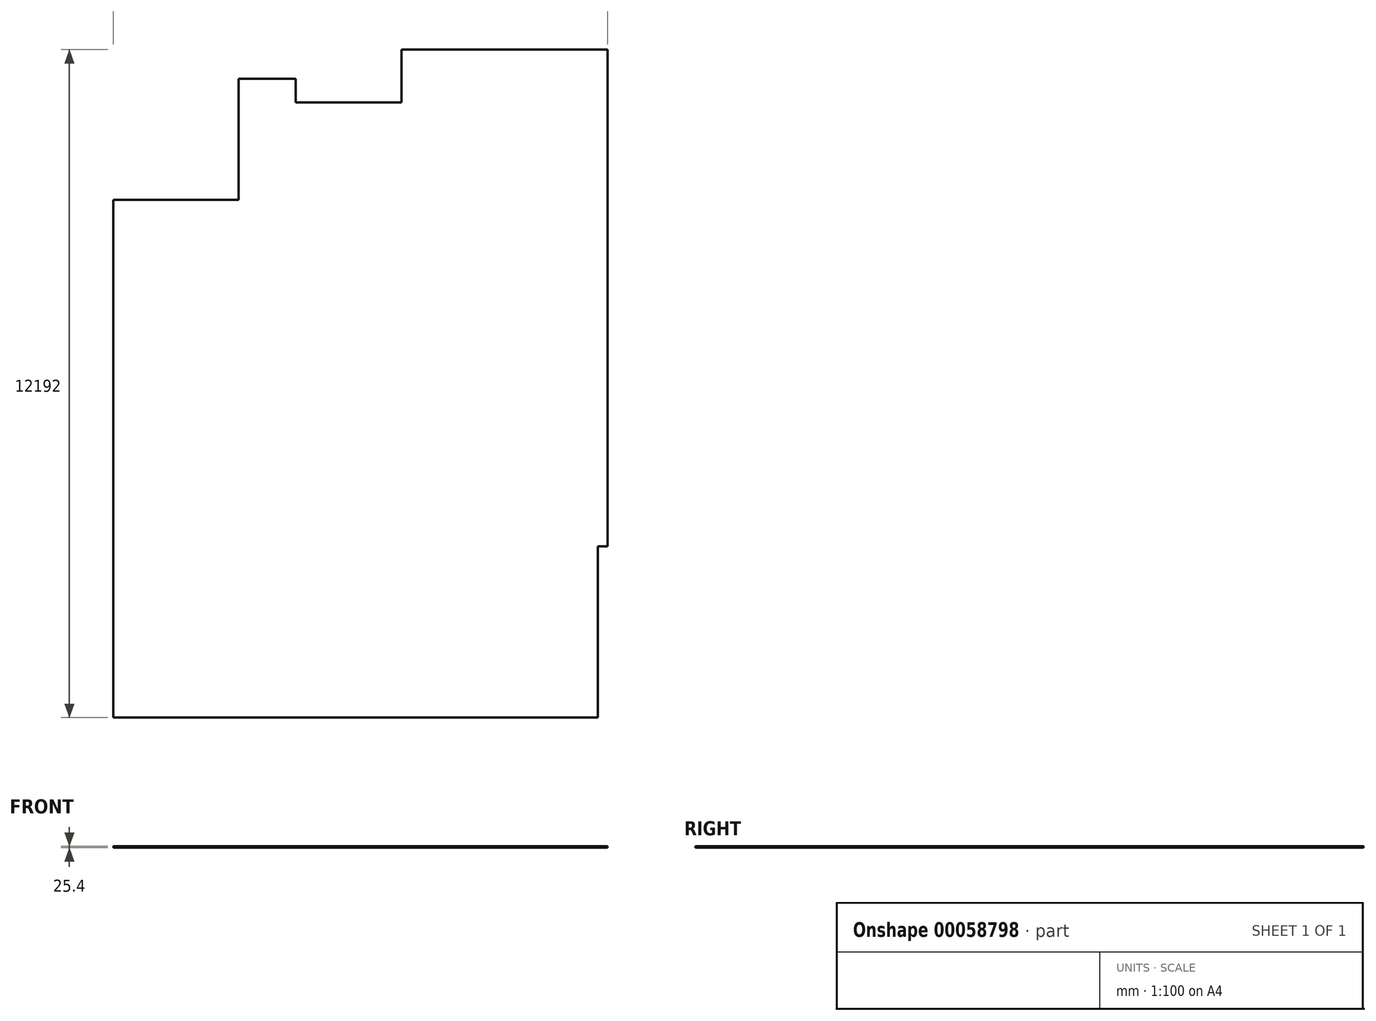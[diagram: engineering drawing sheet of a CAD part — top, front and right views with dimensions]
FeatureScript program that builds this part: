
annotation { "Feature Type Name" : "Feature", "Feature Type Description" : "" }
export const myFeature = defineFeature(function(context is Context, id is Id, definition is map)
    precondition{}
    {
        {
            var Q0;
            Q0=qCreatedBy(makeId("Top.planeOp"),FACE);
            var sketch = newSketch(context, id + "F0", { "sketchPlane" : qUnion([Q0])});
            skLineSegment(sketch, "E0.bottom", {"start": v(0, 0) * mm, "end": v(4749.8, 0) * mm});
            skLineSegment(sketch, "E0.left", {"start": v(0, 0) * mm, "end": v(0, 6604) * mm});
            skLineSegment(sketch, "E1", {"start": v(4749.8, 0) * mm, "end": v(4749.8, 4013.2) * mm});
            skLineSegment(sketch, "E2", {"start": v(0, 6604) * mm, "end": v(4038.6, 6604) * mm});
            skLineSegment(sketch, "E3", {"start": v(4038.6, 8432.8) * mm, "end": v(5257.8, 8432.8) * mm});
            skLineSegment(sketch, "E4", {"start": v(9017, 12192) * mm, "end": v(9017, 10972.8) * mm});
            skLineSegment(sketch, "E5", {"start": v(6451.6, 10972.8) * mm, "end": v(6451.6, 8407.4) * mm});
            skLineSegment(sketch, "E6", {"start": v(6451.6, 8407.4) * mm, "end": v(9017, 8407.4) * mm});
            skLineSegment(sketch, "E7", {"start": v(9017, 8407.4) * mm, "end": v(9017, 5638.8) * mm});
            skLineSegment(sketch, "E8", {"start": v(9017, 5638.8) * mm, "end": v(6451.6, 5638.8) * mm});
            skLineSegment(sketch, "E9", {"start": v(6451.6, 5638.8) * mm, "end": v(6451.6, 4013.2) * mm});
            skLineSegment(sketch, "E10", {"start": v(4749.8, 0) * mm, "end": v(8839.2, 0) * mm});
            skLineSegment(sketch, "E11", {"start": v(8839.2, 0) * mm, "end": v(8839.2, 3124.2) * mm});
            skLineSegment(sketch, "E12", {"start": v(8839.2, 3124.2) * mm, "end": v(7289.8, 3124.2) * mm});
            skLineSegment(sketch, "E13", {"start": v(7289.8, 3124.2) * mm, "end": v(7289.8, 4013.2) * mm});
            skLineSegment(sketch, "E14", {"start": v(9017, 5638.8) * mm, "end": v(9017, 3124.2) * mm});
            skLineSegment(sketch, "E15", {"start": v(8839.2, 3124.2) * mm, "end": v(9017, 3124.2) * mm});
            skLineSegment(sketch, "E16", {"start": v(7289.8, 4013.2) * mm, "end": v(9017, 4013.2) * mm});
            skLineSegment(sketch, "E17", {"start": v(0, 6604) * mm, "end": v(0, 9448.8) * mm});
            skLineSegment(sketch, "E18", {"start": v(3784.6, 9448.8) * mm, "end": v(3784.6, 8305.8) * mm});
            skLineSegment(sketch, "E19", {"start": v(3784.6, 8305.8) * mm, "end": v(4038.6, 8305.8) * mm});
            skLineSegment(sketch, "E20", {"start": v(5257.8, 11226.8) * mm, "end": v(3327.4, 11226.8) * mm});
            skLineSegment(sketch, "E21", {"start": v(3327.4, 11226.8) * mm, "end": v(3327.4, 11658.6) * mm});
            skLineSegment(sketch, "E22", {"start": v(3327.4, 11658.6) * mm, "end": v(2286, 11658.6) * mm});
            skLineSegment(sketch, "E23", {"start": v(2286, 11658.6) * mm, "end": v(2286, 9448.8) * mm});
            skLineSegment(sketch, "E24", {"start": v(3784.6, 9448.8) * mm, "end": v(5257.8, 9448.8) * mm});
            skLineSegment(sketch, "E25", {"start": v(7340.6, 8407.4) * mm, "end": v(7340.6, 9321.8) * mm});
            skLineSegment(sketch, "E26", {"start": v(7340.6, 9321.8) * mm, "end": v(6451.6, 9321.8) * mm});
            skLineSegment(sketch, "E27", {"start": v(7340.6, 9321.8) * mm, "end": v(7340.6, 10972.8) * mm});
            skLineSegment(sketch, "E28", {"start": v(9017, 10972.8) * mm, "end": v(9017, 8407.4) * mm});
            skLineSegment(sketch, "E29", {"start": v(4038.6, 8305.8) * mm, "end": v(4038.6, 7569.2) * mm});
            skLineSegment(sketch, "E30", {"start": v(4038.6, 6604) * mm, "end": v(4038.6, 6934.2) * mm});
            skLineSegment(sketch, "E31", {"start": v(4038.6, 8432.8) * mm, "end": v(4038.6, 8305.8) * mm});
            skLineSegment(sketch, "E32", {"start": v(4749.8, 4013.2) * mm, "end": v(5003.8, 4013.2) * mm});
            skLineSegment(sketch, "E33", {"start": v(6451.6, 4013.2) * mm, "end": v(5791.2, 4013.2) * mm});
            skLineSegment(sketch, "E34", {"start": v(6451.6, 4013.2) * mm, "end": v(6629.4, 4013.2) * mm});
            skLineSegment(sketch, "E35", {"start": v(0, 9448.8) * mm, "end": v(3073.4, 9448.8) * mm});
            skLineSegment(sketch, "E36", {"start": v(5257.8, 8432.8) * mm, "end": v(5257.8, 10337.8) * mm});
            skLineSegment(sketch, "E37", {"start": v(5257.8, 12192) * mm, "end": v(5257.8, 11023.6) * mm});
            skLineSegment(sketch, "E38", {"start": v(8077.2, 10972.8) * mm, "end": v(6451.6, 10972.8) * mm});
            skLineSegment(sketch, "E39", {"start": v(5257.8, 12192) * mm, "end": v(8077.2, 12192) * mm});
            skLineSegment(sketch, "E40", {"start": v(8077.2, 12192) * mm, "end": v(9017, 12192) * mm});
            skLineSegment(sketch, "E41", {"start": v(6451.6, 8407.4) * mm, "end": v(6451.6, 7747) * mm});
            skLineSegment(sketch, "E42", {"start": v(6451.6, 7747) * mm, "end": v(8356.6, 7747) * mm});
            skLineSegment(sketch, "E43", {"start": v(8356.6, 7747) * mm, "end": v(8356.6, 5638.8) * mm});
            skSolve(sketch);
        }
        {
            var Q0;
            Q0=makeQuery(id+"F0.imprint","IMPRINT",FACE,{"disambiguationData":[TD([[makeQuery(id+"F0.imprint","IMPRINT",EDGE,{"derivedFrom":sQuery(id+"F0.wireOp",EDGE,"E0.bottom")}),1.0]])]});
            var Q1;
            {var subQ1=sQuery(id+"F0.wireOp",EDGE,"E3");Q1=makeQuery(id+"F0.imprint","IMPRINT",FACE,{"disambiguationData":[TD([[makeQuery(id+"F0.imprint","IMPRINT",EDGE,{"derivedFrom":subQ1}),1.0]])]});}
            var Q2;
            {var subQ3=sQuery(id+"F0.wireOp",EDGE,"E26");Q2=makeQuery(id+"F0.imprint","IMPRINT",FACE,{"disambiguationData":[TD([[makeQuery(id+"F0.imprint","IMPRINT",EDGE,{"derivedFrom":subQ3}),-1.0]])]});}
            var Q3;
            {var subQ4=sQuery(id+"F0.wireOp",EDGE,"E25");Q3=makeQuery(id+"F0.imprint","IMPRINT",FACE,{"disambiguationData":[TD([[makeQuery(id+"F0.imprint","IMPRINT",EDGE,{"derivedFrom":subQ4}),1.0]])]});}
            var Q4;
            {var subQ1=sQuery(id+"F0.wireOp",EDGE,"E7");Q4=makeQuery(id+"F0.imprint","IMPRINT",FACE,{"disambiguationData":[TD([[makeQuery(id+"F0.imprint","IMPRINT",EDGE,{"derivedFrom":subQ1}),-1.0]])]});}
            var Q5;
            Q5=makeQuery(id+"F0.imprint","IMPRINT",FACE,{"disambiguationData":[TD([[makeQuery(id+"F0.imprint","IMPRINT",EDGE,{"derivedFrom":sQuery(id+"F0.wireOp",EDGE,"E12")}),-1.0]])]});
            extrude(context, id + "F1", {"entities" : qUnion([Q0, Q1, Q2, Q3, Q4, Q5]), "depth" : 25.4 * mm});
        }
    });
